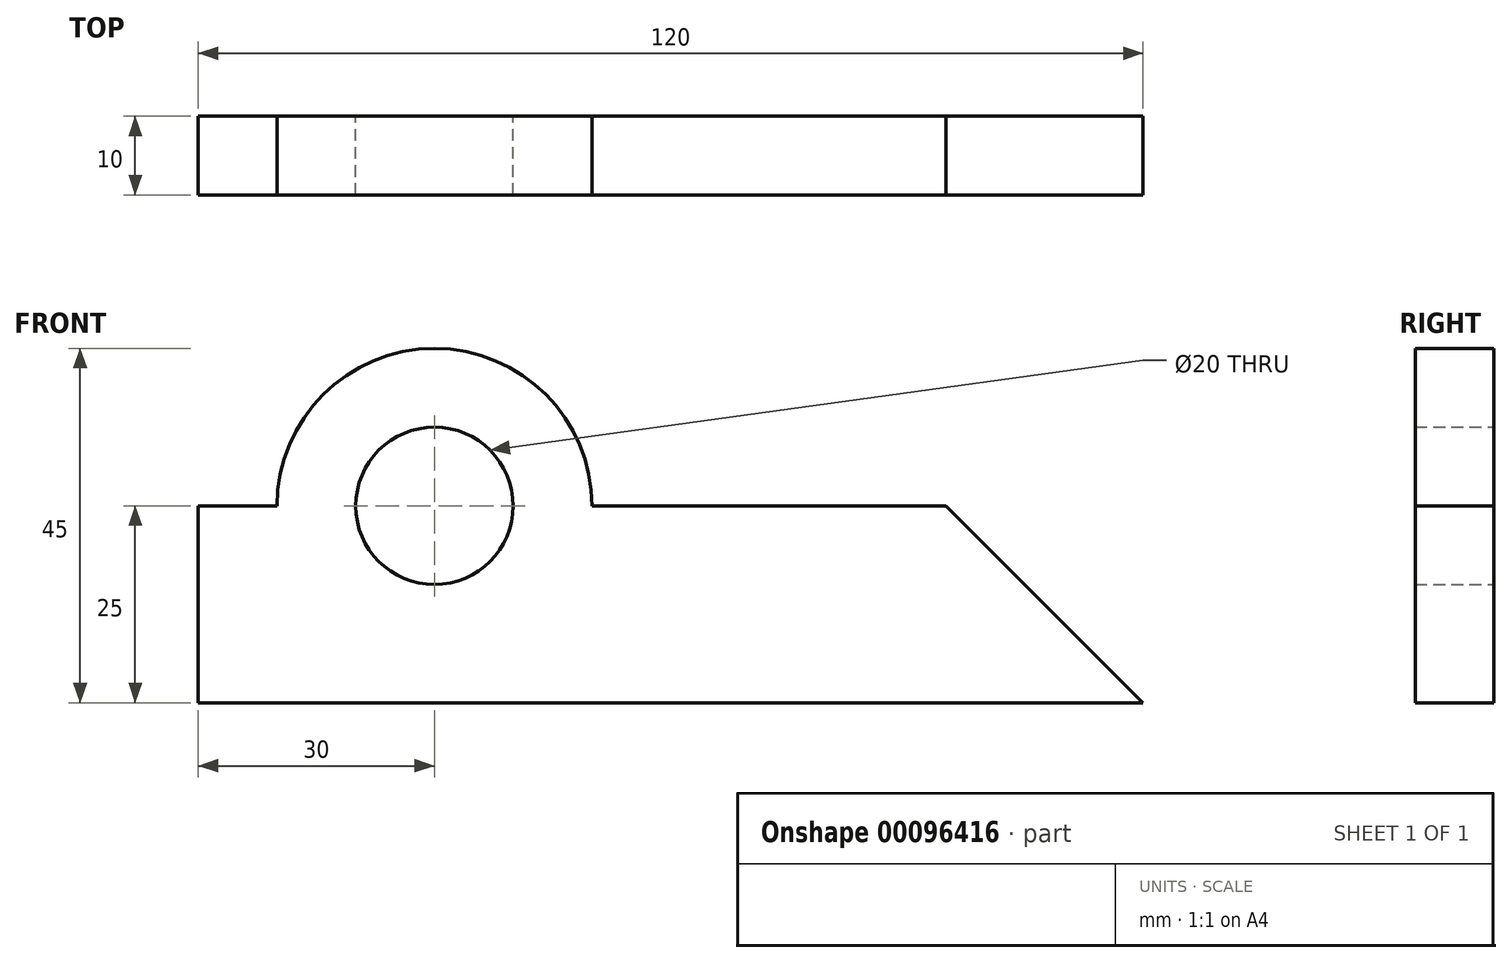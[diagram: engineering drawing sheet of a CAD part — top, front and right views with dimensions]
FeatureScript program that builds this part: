
annotation { "Feature Type Name" : "Feature", "Feature Type Description" : "" }
export const myFeature = defineFeature(function(context is Context, id is Id, definition is map)
    precondition{}
    {
        {
            var Q0;
            Q0=qCreatedBy(makeId("Front.planeOp"),FACE);
            var sketch = newSketch(context, id + "F0", { "sketchPlane" : qUnion([Q0])});
            skLineSegment(sketch, "E0", {"start": v(0, 25) * mm, "end": v(0, 0) * mm});
            skLineSegment(sketch, "E1", {"start": v(0, 0) * mm, "end": v(120, 0) * mm});
            skLineSegment(sketch, "E2", {"start": v(120, 0) * mm, "end": v(95, 25) * mm});
            skLineSegment(sketch, "E3", {"start": v(95, 25) * mm, "end": v(50, 25) * mm});
            skLineSegment(sketch, "E4", {"start": v(0, 25) * mm, "end": v(10, 25) * mm});
            skArc(sketch, "E5", {"start": v(50, 25) * mm, "mid": v(30, 45) * mm, "end": v(10, 25) * mm});
            skCircle(sketch, "E6", {"center": v(30, 25) * mm, "radius": 10 * mm});
            skSolve(sketch);
        }
        {
            var Q0;
            Q0 = qSketchRegion(id + "F0", true);
            extrude(context, id + "F1", {"entities" : qUnion([Q0]), "depth" : 10 * mm});
        }
    });
